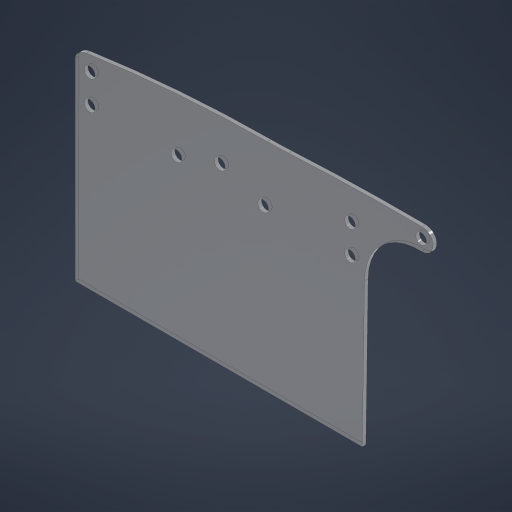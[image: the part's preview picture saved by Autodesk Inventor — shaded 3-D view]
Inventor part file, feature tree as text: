
AUTODESK INVENTOR PART (.ipt)
format: ipt  version: 2024 (Build 280153000, 153)  size: 266,752 bytes
history: native  units: in
note: dims shown in document units (in); Inventor stores cm internally (conversion verified against a paired STEP export)
features: sketch x3, extrude x1, hole x1, other x1
ambient origin geometry x8: Origin, YZ Plane, XZ Plane, XY Plane, X Axis, Y Axis, Z Axis, Center Point
bodies: Solid1 (feature_tree)
feature tree (6):
  extrude  "Extrusion1"  Depth=0.0625in
  hole  "Hole1"  [1 undecoded]
  other  "Bend Part1"
  sketch  "Sketch1"  dims[d2=0.0625in d3=0.0in d4=0.5in]
  sketch  "Sketch2"  dims[d5=0.25in d6=0.5in]
  sketch  "Sketch3"  dims[d7=4.5in d8=0.1875in d9=0.75in d10=0.375in d11=0.25in d12=0.5635in d13=1.0in d14=0.8108in d15=0.25in d23=1.0in d24=1.0in d25=0.25in d27=0.0in d28=1.5in d29=0.125in d31=0.125in d32=0.125in d33=0.98in d34=1.5in d35=1.5in d36=1.25in d37=0.25in d38=45.0deg d39=0.375in d40=8.0in d41=1.0in d42=2.5in]
note: 1 required parameter value undecoded (feature->parameter linkage not recoverable at this tier; creation-order binding heuristic only, values carry confidence <= 0.55)
